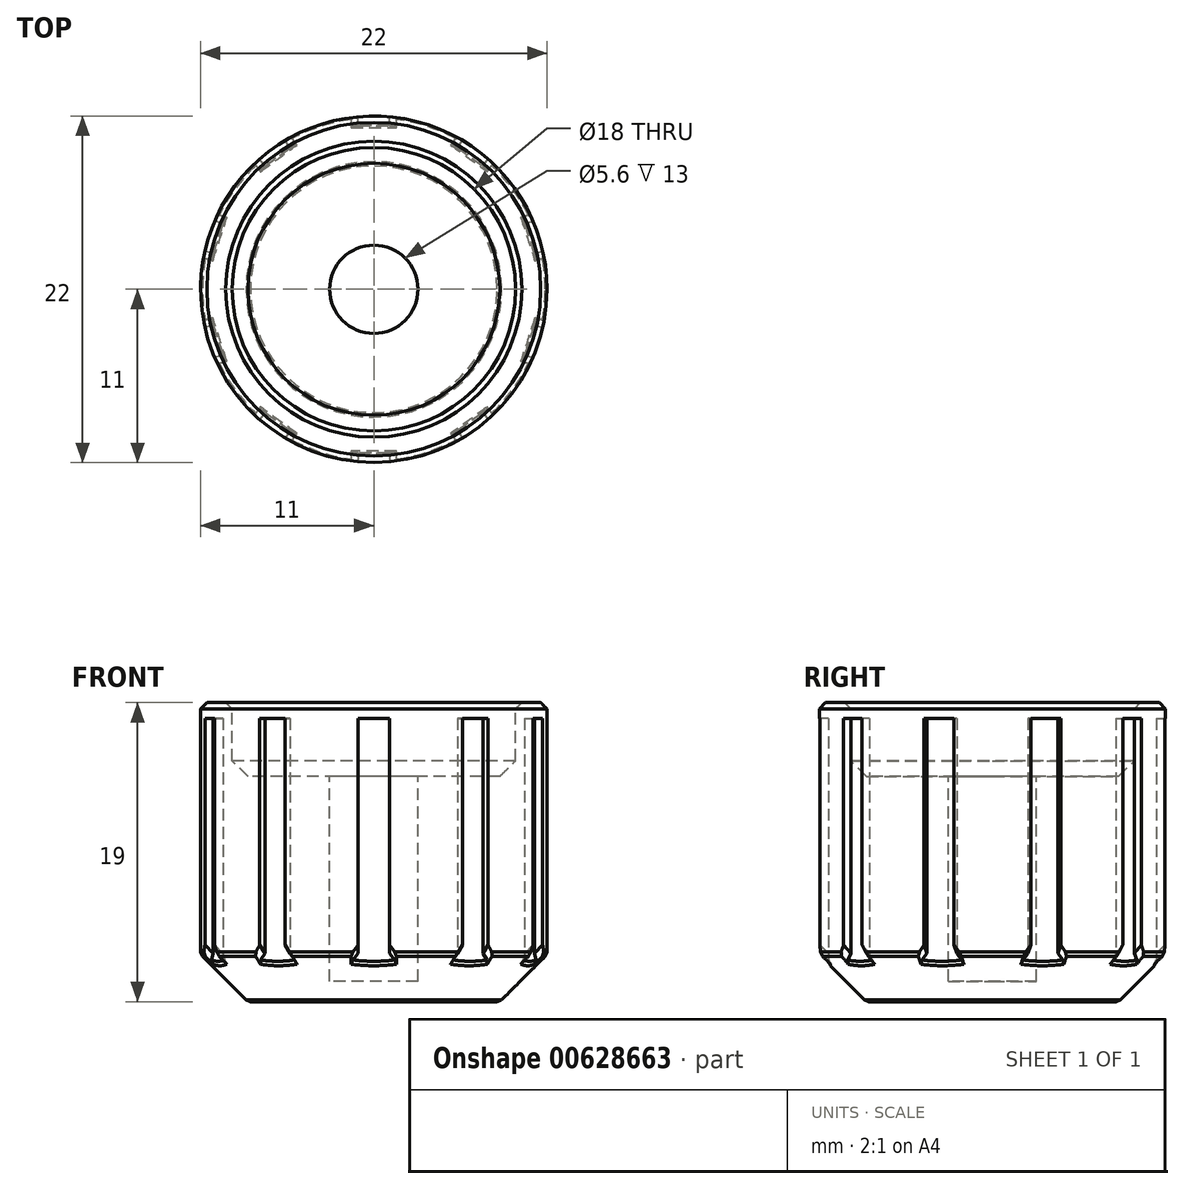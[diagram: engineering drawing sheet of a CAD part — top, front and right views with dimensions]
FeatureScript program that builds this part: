
annotation { "Feature Type Name" : "Feature", "Feature Type Description" : "" }
export const myFeature = defineFeature(function(context is Context, id is Id, definition is map)
    precondition{}
    {
        {
            var Q0;
            Q0=qCreatedBy(makeId("Top.planeOp"),FACE);
            var sketch = newSketch(context, id + "F0", { "sketchPlane" : qUnion([Q0])});
            skCircle(sketch, "E0", {"center": v(0, 0) * mm, "radius": 11 * mm});
            skSolve(sketch);
        }
        {
            var Q0;
            Q0=makeQuery(id+"F0.imprint","IMPRINT",FACE,{"disambiguationData":[TD([[makeQuery(id+"F0.imprint","IMPRINT",EDGE,{"derivedFrom":sQuery(id+"F0.wireOp",EDGE,"E0")}),1.0]])]});
            extrude(context, id + "F1", {"entities" : qUnion([Q0]), "depth" : 19 * mm, "offsetDistance" : 25 * mm});
        }
        {
            var Q0;
            Q0=makeQuery(id+"F1.opExtrude","CAP_FACE",FACE,{"disambiguationData":[OSD([sQuery(id+"F0.wireOp",EDGE,"E0")])],"isStart":false});
            var sketch = newSketch(context, id + "F2", { "sketchPlane" : qUnion([Q0])});
            skCircle(sketch, "E1.0", {"center": v(0, 0) * mm, "radius": 9 * mm});
            skSolve(sketch);
        }
        {
            var Q0;
            Q0=makeQuery(id+"F2.imprint","IMPRINT",FACE,{"disambiguationData":[TD([[makeQuery(id+"F2.imprint","IMPRINT",EDGE,{"derivedFrom":sQuery(id+"F2.wireOp",EDGE,"E1.0")}),1.0]])]});
            extrude(context, id + "F3", {"entities" : qUnion([Q0]), "operationType" : NewBodyOperationType.REMOVE, "oppositeDirection" : true, "depth" : 4.7 * mm, "offsetDistance" : 25 * mm});
        }
        {
            var Q0;
            Q0=makeQuery(id+"F3.boolean.opBoolean","COPY",FACE,{"derivedFrom":makeQuery(id+"F3.opExtrude","CAP_FACE",FACE,{"disambiguationData":[OSD([sQuery(id+"F2.wireOp",EDGE,"E1.0")])],"isStart":false})});
            var sketch = newSketch(context, id + "F4", { "sketchPlane" : qUnion([Q0])});
            skCircle(sketch, "E2", {"center": v(0, 0) * mm, "radius": 2.8 * mm});
            skSolve(sketch);
        }
        {
            var Q0;
            Q0=makeQuery(id+"F4.imprint","IMPRINT",FACE,{"disambiguationData":[TD([[makeQuery(id+"F4.imprint","IMPRINT",EDGE,{"derivedFrom":sQuery(id+"F4.wireOp",EDGE,"E2")}),1.0]])]});
            extrude(context, id + "F5", {"entities" : qUnion([Q0]), "operationType" : NewBodyOperationType.REMOVE, "oppositeDirection" : true, "depth" : 13 * mm, "offsetDistance" : 25 * mm});
        }
        {
            var Q0;
            Q0=makeQuery(id+"F1.opExtrude","CAP_EDGE",EDGE,{"disambiguationData":[OSD([sQuery(id+"F0.wireOp",EDGE,"E0")])],"isStart":true});
            chamfer(context, id + "F6", {"entities" : qUnion([Q0]), "width" : 3 * mm, "tangentPropagation" : true});
        }
        {
            var Q0;
            Q0=makeQuery(id+"F1.opExtrude","CAP_FACE",FACE,{"disambiguationData":[OSD([sQuery(id+"F0.wireOp",EDGE,"E0")])],"isStart":true});
            var sketch = newSketch(context, id + "F7", { "sketchPlane" : qUnion([Q0])});
            skCircle(sketch, "E3.0", {"center": v(0, 0) * mm, "radius": 11 * mm, "construction": true});
            skLineSegment(sketch, "E4", {"start": v(0, 0) * mm, "end": v(0, 11) * mm, "construction": true});
            skLineSegment(sketch, "E5.bottom", {"start": v(1, 10.4) * mm, "end": v(-1, 10.4) * mm});
            skLineSegment(sketch, "E5.top", {"start": v(1, 11.6) * mm, "end": v(-1, 11.6) * mm});
            skLineSegment(sketch, "E5.left", {"start": v(1, 10.4) * mm, "end": v(1, 11.6) * mm});
            skLineSegment(sketch, "E5.right", {"start": v(-1, 10.4) * mm, "end": v(-1, 11.6) * mm});
            skPoint(sketch, "E5.middle", {"position": v(0, 11) * mm});
            skLineSegment(sketch, "E6.1.0", {"start": v(-6, 9.97) * mm, "end": v(-7.63, 8.8) * mm});
            skLineSegment(sketch, "E6.1.1", {"start": v(-5.3, 9) * mm, "end": v(-6, 9.97) * mm});
            skLineSegment(sketch, "E6.1.2", {"start": v(-5.3, 9) * mm, "end": v(-6.92, 7.83) * mm});
            skLineSegment(sketch, "E6.1.3", {"start": v(-6.92, 7.83) * mm, "end": v(-7.63, 8.8) * mm});
            skLineSegment(sketch, "E6.2.0", {"start": v(-10.72, 4.54) * mm, "end": v(-11.34, 2.63) * mm});
            skLineSegment(sketch, "E6.2.1", {"start": v(-9.58, 4.16) * mm, "end": v(-10.72, 4.54) * mm});
            skLineSegment(sketch, "E6.2.2", {"start": v(-9.58, 4.16) * mm, "end": v(-10.2, 2.26) * mm});
            skLineSegment(sketch, "E6.2.3", {"start": v(-10.2, 2.26) * mm, "end": v(-11.34, 2.63) * mm});
            skLineSegment(sketch, "E6.3.0", {"start": v(-11.34, -2.63) * mm, "end": v(-10.72, -4.54) * mm});
            skLineSegment(sketch, "E6.3.1", {"start": v(-10.2, -2.26) * mm, "end": v(-11.34, -2.63) * mm});
            skLineSegment(sketch, "E6.3.2", {"start": v(-10.2, -2.26) * mm, "end": v(-9.58, -4.16) * mm});
            skLineSegment(sketch, "E6.3.3", {"start": v(-9.58, -4.16) * mm, "end": v(-10.72, -4.54) * mm});
            skLineSegment(sketch, "E6.4.0", {"start": v(-7.63, -8.8) * mm, "end": v(-6, -9.97) * mm});
            skLineSegment(sketch, "E6.4.1", {"start": v(-6.92, -7.83) * mm, "end": v(-7.63, -8.8) * mm});
            skLineSegment(sketch, "E6.4.2", {"start": v(-6.92, -7.83) * mm, "end": v(-5.3, -9) * mm});
            skLineSegment(sketch, "E6.4.3", {"start": v(-5.3, -9) * mm, "end": v(-6, -9.97) * mm});
            skLineSegment(sketch, "E6.5.0", {"start": v(-1, -11.6) * mm, "end": v(1, -11.6) * mm});
            skLineSegment(sketch, "E6.5.1", {"start": v(-1, -10.4) * mm, "end": v(-1, -11.6) * mm});
            skLineSegment(sketch, "E6.5.2", {"start": v(-1, -10.4) * mm, "end": v(1, -10.4) * mm});
            skLineSegment(sketch, "E6.5.3", {"start": v(1, -10.4) * mm, "end": v(1, -11.6) * mm});
            skLineSegment(sketch, "E6.6.0", {"start": v(6, -9.97) * mm, "end": v(7.63, -8.8) * mm});
            skLineSegment(sketch, "E6.6.1", {"start": v(5.3, -9) * mm, "end": v(6, -9.97) * mm});
            skLineSegment(sketch, "E6.6.2", {"start": v(5.3, -9) * mm, "end": v(6.92, -7.83) * mm});
            skLineSegment(sketch, "E6.6.3", {"start": v(6.92, -7.83) * mm, "end": v(7.63, -8.8) * mm});
            skLineSegment(sketch, "E6.7.0", {"start": v(10.72, -4.54) * mm, "end": v(11.34, -2.63) * mm});
            skLineSegment(sketch, "E6.7.1", {"start": v(9.58, -4.16) * mm, "end": v(10.72, -4.54) * mm});
            skLineSegment(sketch, "E6.7.2", {"start": v(9.58, -4.16) * mm, "end": v(10.2, -2.26) * mm});
            skLineSegment(sketch, "E6.7.3", {"start": v(10.2, -2.26) * mm, "end": v(11.34, -2.63) * mm});
            skLineSegment(sketch, "E6.8.0", {"start": v(11.34, 2.63) * mm, "end": v(10.72, 4.54) * mm});
            skLineSegment(sketch, "E6.8.1", {"start": v(10.2, 2.26) * mm, "end": v(11.34, 2.63) * mm});
            skLineSegment(sketch, "E6.8.2", {"start": v(10.2, 2.26) * mm, "end": v(9.58, 4.16) * mm});
            skLineSegment(sketch, "E6.8.3", {"start": v(9.58, 4.16) * mm, "end": v(10.72, 4.54) * mm});
            skLineSegment(sketch, "E6.9.0", {"start": v(7.63, 8.8) * mm, "end": v(6, 9.97) * mm});
            skLineSegment(sketch, "E6.9.1", {"start": v(6.92, 7.83) * mm, "end": v(7.63, 8.8) * mm});
            skLineSegment(sketch, "E6.9.2", {"start": v(6.92, 7.83) * mm, "end": v(5.3, 9) * mm});
            skLineSegment(sketch, "E6.9.3", {"start": v(5.3, 9) * mm, "end": v(6, 9.97) * mm});
            skSolve(sketch);
        }
        {
            var Q0;
            Q0=makeQuery(id+"F7.imprint","IMPRINT",FACE,{"disambiguationData":[TD([[makeQuery(id+"F7.imprint","IMPRINT",EDGE,{"derivedFrom":sQuery(id+"F7.wireOp",EDGE,"E5.bottom")}),-1.0]])]});
            var Q1;
            Q1=makeQuery(id+"F7.imprint","IMPRINT",FACE,{"disambiguationData":[TD([[makeQuery(id+"F7.imprint","IMPRINT",EDGE,{"derivedFrom":sQuery(id+"F7.wireOp",EDGE,"E6.9.0")}),1.0]])]});
            var Q2;
            Q2=makeQuery(id+"F7.imprint","IMPRINT",FACE,{"disambiguationData":[TD([[makeQuery(id+"F7.imprint","IMPRINT",EDGE,{"derivedFrom":sQuery(id+"F7.wireOp",EDGE,"E6.8.0")}),1.0]])]});
            var Q3;
            Q3=makeQuery(id+"F7.imprint","IMPRINT",FACE,{"disambiguationData":[TD([[makeQuery(id+"F7.imprint","IMPRINT",EDGE,{"derivedFrom":sQuery(id+"F7.wireOp",EDGE,"E6.7.0")}),1.0]])]});
            var Q4;
            Q4=makeQuery(id+"F7.imprint","IMPRINT",FACE,{"disambiguationData":[TD([[makeQuery(id+"F7.imprint","IMPRINT",EDGE,{"derivedFrom":sQuery(id+"F7.wireOp",EDGE,"E6.6.0")}),1.0]])]});
            var Q5;
            Q5=makeQuery(id+"F7.imprint","IMPRINT",FACE,{"disambiguationData":[TD([[makeQuery(id+"F7.imprint","IMPRINT",EDGE,{"derivedFrom":sQuery(id+"F7.wireOp",EDGE,"E6.5.0")}),1.0]])]});
            var Q6;
            Q6=makeQuery(id+"F7.imprint","IMPRINT",FACE,{"disambiguationData":[TD([[makeQuery(id+"F7.imprint","IMPRINT",EDGE,{"derivedFrom":sQuery(id+"F7.wireOp",EDGE,"E6.4.0")}),1.0]])]});
            var Q7;
            Q7=makeQuery(id+"F7.imprint","IMPRINT",FACE,{"disambiguationData":[TD([[makeQuery(id+"F7.imprint","IMPRINT",EDGE,{"derivedFrom":sQuery(id+"F7.wireOp",EDGE,"E6.3.0")}),1.0]])]});
            var Q8;
            Q8=makeQuery(id+"F7.imprint","IMPRINT",FACE,{"disambiguationData":[TD([[makeQuery(id+"F7.imprint","IMPRINT",EDGE,{"derivedFrom":sQuery(id+"F7.wireOp",EDGE,"E6.2.0")}),1.0]])]});
            var Q9;
            Q9=makeQuery(id+"F7.imprint","IMPRINT",FACE,{"disambiguationData":[TD([[makeQuery(id+"F7.imprint","IMPRINT",EDGE,{"derivedFrom":sQuery(id+"F7.wireOp",EDGE,"E6.1.0")}),1.0]])]});
            var Q10;
            Q10=makeQuery(id+"F1.opExtrude","CAP_FACE",FACE,{"disambiguationData":[OSD([sQuery(id+"F0.wireOp",EDGE,"E0")])],"isStart":false});
            extrude(context, id + "F8", {"entities" : qUnion([Q0, Q1, Q2, Q3, Q4, Q5, Q6, Q7, Q8, Q9]), "operationType" : NewBodyOperationType.REMOVE, "endBound" : BoundingType.UP_TO_SURFACE, "oppositeDirection" : true, "depth" : 25 * mm, "endBoundEntityFace" : qUnion([Q10]), "hasOffset" : true, "offsetDistance" : 1 * mm});
        }
        {
            var Q0;
            Q0=makeQuery(id+"F5.boolean.opBoolean","COPY",EDGE,{"derivedFrom":makeQuery(id+"F5.opExtrude","CAP_EDGE",EDGE,{"disambiguationData":[OSD([sQuery(id+"F4.wireOp",EDGE,"E2")])],"isStart":true})});
            var Q1;
            Q1=makeQuery(id+"F3.boolean.opBoolean","COPY",EDGE,{"derivedFrom":makeQuery(id+"F3.opExtrude","CAP_EDGE",EDGE,{"disambiguationData":[OSD([sQuery(id+"F2.wireOp",EDGE,"E1.0")])],"isStart":false})});
            chamfer(context, id + "F9", {"entities" : qUnion([Q0, Q1]), "width" : 1 * mm, "tangentPropagation" : true});
        }
        {
            var Q0;
            Q0=makeQuery(id+"F1.opExtrude","CAP_FACE",FACE,{"disambiguationData":[OSD([sQuery(id+"F0.wireOp",EDGE,"E0")])],"isStart":false});
            var Q1;
            Q1=makeQuery(id+"F6.opChamfer","BLEND_FACE",FACE,{"disambiguationData":[OSD([sQuery(id+"F0.wireOp",EDGE,"E0")])]});
            chamfer(context, id + "F10", {"entities" : qUnion([Q0, Q1]), "width" : 0.4 * mm, "tangentPropagation" : true});
        }
    });
